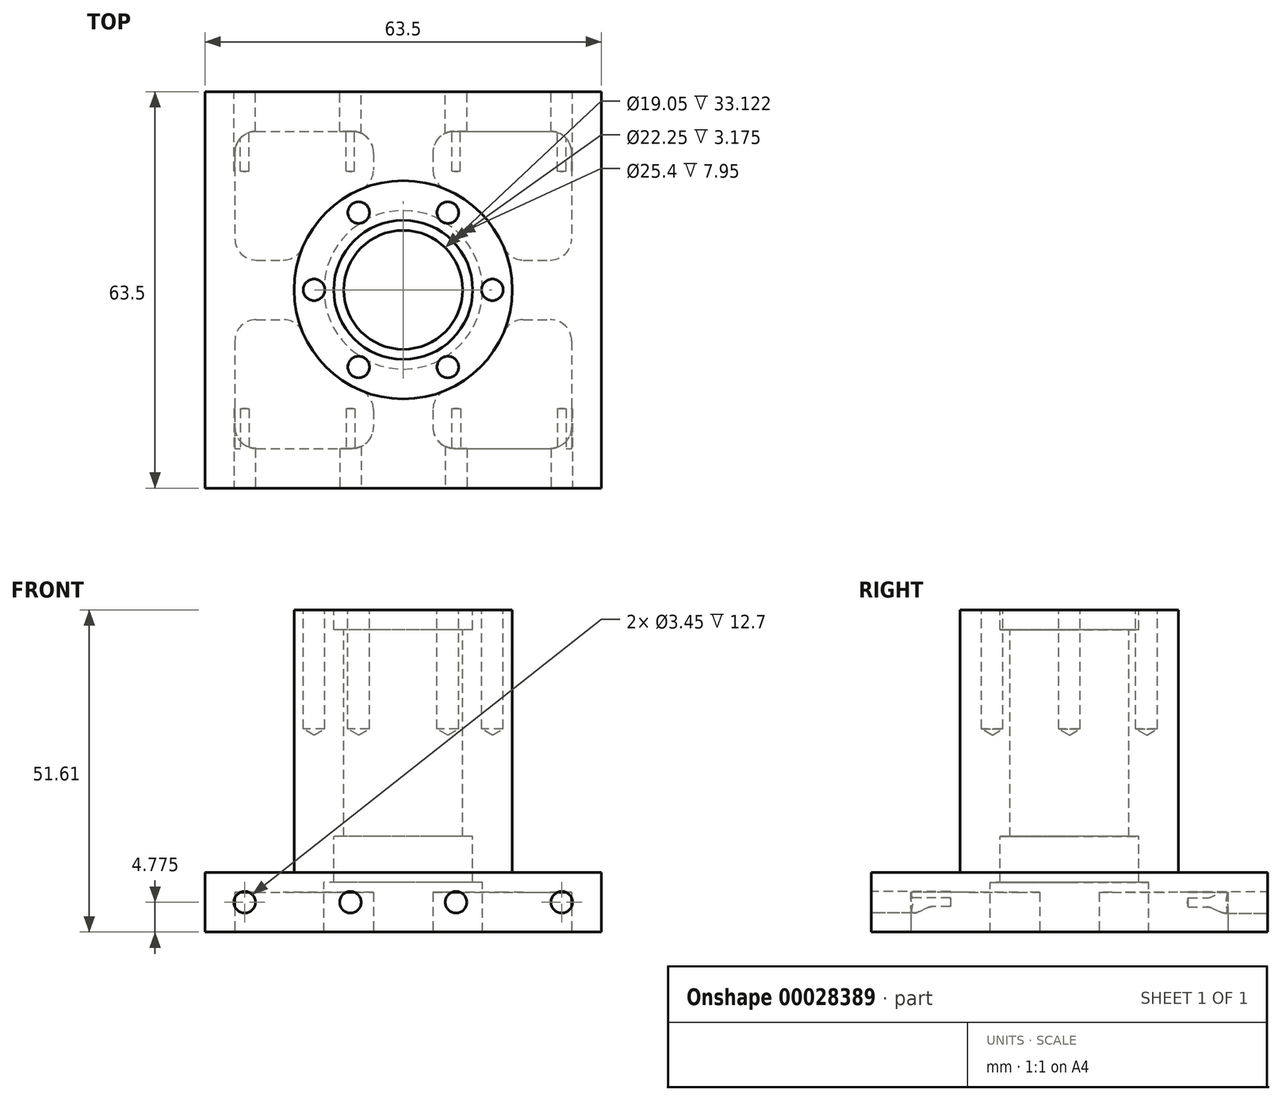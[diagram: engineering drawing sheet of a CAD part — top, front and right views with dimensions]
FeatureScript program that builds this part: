
annotation { "Feature Type Name" : "Feature", "Feature Type Description" : "" }
export const myFeature = defineFeature(function(context is Context, id is Id, definition is map)
    precondition{}
    {
        {
            var Q0;
            Q0=qCreatedBy(makeId("Front.planeOp"),FACE);
            var sketch = newSketch(context, id + "F0", { "sketchPlane" : qUnion([Q0])});
            skLineSegment(sketch, "E0", {"start": v(0, 39.17) * mm, "end": v(0, 0) * mm, "construction": true});
            skLineSegment(sketch, "E1", {"start": v(0, 0) * mm, "end": v(-12.7, 0) * mm, "construction": true});
            skLineSegment(sketch, "E2.bottom", {"start": v(-12.7, 0) * mm, "end": v(-45.72, 0) * mm});
            skLineSegment(sketch, "E2.top", {"start": v(-11.13, 51.61) * mm, "end": v(-17.49, 51.61) * mm});
            skLineSegment(sketch, "E2.left", {"start": v(-9.52, 15.32) * mm, "end": v(-9.53, 48.44) * mm});
            skLineSegment(sketch, "E2.right", {"start": v(-45.72, 0) * mm, "end": v(-45.72, 9.52) * mm});
            skLineSegment(sketch, "E3.top", {"start": v(-11.13, 48.44) * mm, "end": v(-9.53, 48.44) * mm});
            skLineSegment(sketch, "E3.left", {"start": v(-11.13, 51.61) * mm, "end": v(-11.13, 48.44) * mm});
            skLineSegment(sketch, "E4.bottom", {"start": v(-9.53, 15.32) * mm, "end": v(-11.13, 15.32) * mm});
            skLineSegment(sketch, "E4.right", {"start": v(-12.7, 7.95) * mm, "end": v(-12.7, 0) * mm});
            skLineSegment(sketch, "E5.bottom", {"start": v(-11.13, 7.95) * mm, "end": v(-12.7, 7.95) * mm});
            skLineSegment(sketch, "E5.left", {"start": v(-11.13, 7.95) * mm, "end": v(-11.13, 15.32) * mm});
            skLineSegment(sketch, "E6.bottom", {"start": v(-17.49, 9.53) * mm, "end": v(-45.72, 9.52) * mm});
            skLineSegment(sketch, "E6.left", {"start": v(-17.49, 9.53) * mm, "end": v(-17.49, 51.61) * mm});
            skSolve(sketch);
        }
        {
            var Q0;
            Q0=makeQuery(id+"F0.imprint","IMPRINT",FACE,{"disambiguationData":[TD([[makeQuery(id+"F0.imprint","IMPRINT",EDGE,{"derivedFrom":sQuery(id+"F0.wireOp",EDGE,"E2.bottom")}),-1.0]])]});
            var Q1;
            Q1=sQuery(id+"F0.wireOp",EDGE,"E0");
            revolve(context, id + "F1", {"entities" : qUnion([Q0]), "axis" : qUnion([Q1]), "revolveType" : RevolveType.FULL});
        }
        {
            var Q0;
            Q0=makeQuery(id+"F1.opRevolve","SWEPT_FACE",FACE,{"disambiguationData":[OSD([sQuery(id+"F0.wireOp",EDGE,"E2.bottom")])]});
            var sketch = newSketch(context, id + "F2", { "sketchPlane" : qUnion([Q0])});
            skLineSegment(sketch, "E7.rect.bottom", {"start": v(31.75, 31.75) * mm, "end": v(-31.75, 31.75) * mm});
            skLineSegment(sketch, "E7.rect.top", {"start": v(31.75, -31.75) * mm, "end": v(-31.75, -31.75) * mm});
            skLineSegment(sketch, "E7.rect.left", {"start": v(31.75, 31.75) * mm, "end": v(31.75, -31.75) * mm});
            skLineSegment(sketch, "E7.rect.right", {"start": v(-31.75, 31.75) * mm, "end": v(-31.75, -31.75) * mm});
            skPoint(sketch, "E7.rect.middle", {"position": v(0, 0) * mm});
            skSolve(sketch);
        }
        {
            var Q0;
            Q0=makeQuery(id+"F2.imprint","IMPRINT",FACE,{"disambiguationData":[TD([[makeQuery(id+"F2.imprint","IMPRINT",EDGE,{"derivedFrom":sQuery(id+"F2.wireOp",EDGE,"E7.rect.bottom")}),-1.0]])]});
            extrude(context, id + "F3", {"entities" : qUnion([Q0]), "operationType" : NewBodyOperationType.REMOVE, "endBound" : BoundingType.THROUGH_ALL, "oppositeDirection" : true, "depth" : 25.4 * mm});
        }
        {
            var Q0;
            Q0=makeQuery(id+"F3.boolean.opBoolean","COPY",FACE,{"derivedFrom":makeQuery(id+"F3.opExtrude","SWEPT_FACE",FACE,{"disambiguationData":[OSD([sQuery(id+"F2.wireOp",EDGE,"E7.rect.bottom")])]})});
            var sketch = newSketch(context, id + "F4", { "sketchPlane" : qUnion([Q0])});
            skLineSegment(sketch, "E8", {"start": v(-25.4, 4.78) * mm, "end": v(25.4, 4.78) * mm});
            skPoint(sketch, "E9", {"position": v(-8.47, 4.78) * mm});
            skPoint(sketch, "E10", {"position": v(8.47, 4.78) * mm});
            skLineSegment(sketch, "E11", {"start": v(0, 9.52) * mm, "end": v(0, -11.62) * mm});
            skSolve(sketch);
        }
        {
            var Q0;
            Q0=sQuery(id+"F4.wireOp",VERTEX,"E8.start");
            var Q1;
            Q1=sQuery(id+"F4.wireOp",VERTEX,"E9");
            var Q2;
            Q2=sQuery(id+"F4.wireOp",VERTEX,"E10");
            var Q3;
            Q3=sQuery(id+"F4.wireOp",VERTEX,"E8.end");
            var Q4;
            Q4=makeQuery(id+"F1.opRevolve","SWEPT_BODY",BODY,{"disambiguationData":[OSD([sQuery(id+"F0.wireOp",EDGE,"E2.bottom"),sQuery(id+"F0.wireOp",EDGE,"E2.top"),sQuery(id+"F0.wireOp",EDGE,"E2.left"),sQuery(id+"F0.wireOp",EDGE,"E2.right"),sQuery(id+"F0.wireOp",EDGE,"E3.top"),sQuery(id+"F0.wireOp",EDGE,"E3.left"),sQuery(id+"F0.wireOp",EDGE,"E4.bottom"),sQuery(id+"F0.wireOp",EDGE,"E4.right"),sQuery(id+"F0.wireOp",EDGE,"E5.bottom"),sQuery(id+"F0.wireOp",EDGE,"E5.left"),sQuery(id+"F0.wireOp",EDGE,"E6.bottom"),sQuery(id+"F0.wireOp",EDGE,"E6.left")])]});
            hole(context, id + "F5", {"style" : HoleStyle.SIMPLE, "holeDiameter" : 3.45 * mm, "endStyle" : HoleEndStyle.BLIND, "holeDepth" : 12.7 * mm, "locations" : qUnion([Q0, Q1, Q2, Q3]), "scope" : qUnion([Q4])});
        }
        {
            var Q0;
            Q0=makeQuery(id+"F1.opRevolve","SWEPT_FACE",FACE,{"disambiguationData":[OSD([sQuery(id+"F0.wireOp",EDGE,"E2.top")])]});
            var sketch = newSketch(context, id + "F6", { "sketchPlane" : qUnion([Q0])});
            skLineSegment(sketch, "E12", {"start": v(0, 0) * mm, "end": v(14.29, 0) * mm});
            skLineSegment(sketch, "E13.1.0", {"start": v(0, 0) * mm, "end": v(7.14, 12.37) * mm});
            skLineSegment(sketch, "E13.2.0", {"start": v(0, 0) * mm, "end": v(-7.14, 12.37) * mm});
            skLineSegment(sketch, "E13.3.0", {"start": v(0, 0) * mm, "end": v(-14.29, 0) * mm});
            skLineSegment(sketch, "E13.4.0", {"start": v(0, 0) * mm, "end": v(-7.14, -12.37) * mm});
            skLineSegment(sketch, "E13.5.0", {"start": v(0, 0) * mm, "end": v(7.14, -12.37) * mm});
            skPoint(sketch, "E13.center", {"position": v(0, 0) * mm});
            skSolve(sketch);
        }
        {
            var Q0;
            Q0=sQuery(id+"F6.wireOp",VERTEX,"E12.end");
            var Q1;
            Q1=sQuery(id+"F6.wireOp",VERTEX,"E13.5.0.end");
            var Q2;
            Q2=sQuery(id+"F6.wireOp",VERTEX,"E13.4.0.end");
            var Q3;
            Q3=sQuery(id+"F6.wireOp",VERTEX,"E13.3.0.end");
            var Q4;
            Q4=sQuery(id+"F6.wireOp",VERTEX,"E13.2.0.end");
            var Q5;
            Q5=sQuery(id+"F6.wireOp",VERTEX,"E13.1.0.end");
            var Q6;
            Q6=makeQuery(id+"F1.opRevolve","SWEPT_BODY",BODY,{"disambiguationData":[OSD([sQuery(id+"F0.wireOp",EDGE,"E2.bottom"),sQuery(id+"F0.wireOp",EDGE,"E2.top"),sQuery(id+"F0.wireOp",EDGE,"E2.left"),sQuery(id+"F0.wireOp",EDGE,"E2.right"),sQuery(id+"F0.wireOp",EDGE,"E3.top"),sQuery(id+"F0.wireOp",EDGE,"E3.left"),sQuery(id+"F0.wireOp",EDGE,"E4.bottom"),sQuery(id+"F0.wireOp",EDGE,"E4.right"),sQuery(id+"F0.wireOp",EDGE,"E5.bottom"),sQuery(id+"F0.wireOp",EDGE,"E5.left"),sQuery(id+"F0.wireOp",EDGE,"E6.bottom"),sQuery(id+"F0.wireOp",EDGE,"E6.left")])]});
            hole(context, id + "F7", {"style" : HoleStyle.SIMPLE, "holeDiameter" : 3.45 * mm, "endStyle" : HoleEndStyle.BLIND, "holeDepth" : 19.05 * mm, "locations" : qUnion([Q0, Q1, Q2, Q3, Q4, Q5]), "scope" : qUnion([Q6])});
        }
        {
            var Q0;
            Q0=makeQuery(id+"F1.opRevolve","SWEPT_FACE",FACE,{"disambiguationData":[OSD([sQuery(id+"F0.wireOp",EDGE,"E2.bottom")])]});
            var sketch = newSketch(context, id + "F8", { "sketchPlane" : qUnion([Q0])});
            skLineSegment(sketch, "E14.rect.bottom", {"start": v(-26.97, -25.4) * mm, "end": v(-4.76, -25.4) * mm});
            skLineSegment(sketch, "E14.rect.top", {"start": v(-26.97, 25.4) * mm, "end": v(-4.76, 25.4) * mm});
            skLineSegment(sketch, "E14.rect.left", {"start": v(-26.97, -25.4) * mm, "end": v(-26.97, -4.76) * mm});
            skLineSegment(sketch, "E14.rect.right", {"start": v(26.97, -25.4) * mm, "end": v(26.97, -4.76) * mm});
            skPoint(sketch, "E14.rect.middle", {"position": v(0, 0) * mm});
            skArc(sketch, "E15", {"start": v(-4.76, 16.81) * mm, "mid": v(-12.36, 12.36) * mm, "end": v(-16.81, 4.76) * mm});
            skLineSegment(sketch, "E16", {"start": v(-33.58, 0) * mm, "end": v(0, 0) * mm, "construction": true});
            skLineSegment(sketch, "E17", {"start": v(0, 36.76) * mm, "end": v(0, 0) * mm, "construction": true});
            skLineSegment(sketch, "E18.bottom", {"start": v(-26.97, -4.76) * mm, "end": v(-16.81, -4.76) * mm});
            skLineSegment(sketch, "E18.top", {"start": v(-26.97, 4.76) * mm, "end": v(-16.81, 4.76) * mm});
            skLineSegment(sketch, "E19.left", {"start": v(-4.76, 16.81) * mm, "end": v(-4.76, 25.4) * mm});
            skLineSegment(sketch, "E19.right", {"start": v(4.76, 16.81) * mm, "end": v(4.76, 25.4) * mm});
            skLineSegment(sketch, "E20.bottom", {"start": v(16.81, 4.76) * mm, "end": v(26.97, 4.76) * mm});
            skLineSegment(sketch, "E20.top", {"start": v(16.81, -4.76) * mm, "end": v(26.97, -4.76) * mm});
            skLineSegment(sketch, "E21.left", {"start": v(-4.76, -25.4) * mm, "end": v(-4.76, -16.81) * mm});
            skLineSegment(sketch, "E21.right", {"start": v(4.76, -25.4) * mm, "end": v(4.76, -16.81) * mm});
            skLineSegment(sketch, "E22.trimOffspring", {"start": v(4.76, 25.4) * mm, "end": v(26.97, 25.4) * mm});
            skArc(sketch, "E23.trimOffspring", {"start": v(16.81, 4.76) * mm, "mid": v(12.36, 12.36) * mm, "end": v(4.76, 16.81) * mm});
            skLineSegment(sketch, "E24.trimOffspring", {"start": v(4.76, -25.4) * mm, "end": v(26.97, -25.4) * mm});
            skArc(sketch, "E25.trimOffspring", {"start": v(4.76, -16.81) * mm, "mid": v(12.36, -12.36) * mm, "end": v(16.81, -4.76) * mm});
            skLineSegment(sketch, "E26.trimOffspring", {"start": v(-26.97, 4.76) * mm, "end": v(-26.97, 25.4) * mm});
            skArc(sketch, "E27.trimOffspring", {"start": v(-16.81, -4.76) * mm, "mid": v(-12.36, -12.36) * mm, "end": v(-4.76, -16.81) * mm});
            skLineSegment(sketch, "E28.trimOffspring", {"start": v(26.97, 4.76) * mm, "end": v(26.97, 25.4) * mm});
            skSolve(sketch);
        }
        {
            var Q0;
            Q0=makeQuery(id+"F8.imprint","IMPRINT",FACE,{"disambiguationData":[TD([[makeQuery(id+"F8.imprint","IMPRINT",EDGE,{"derivedFrom":sQuery(id+"F8.wireOp",EDGE,"E14.rect.bottom")}),1.0]])]});
            var Q1;
            Q1=makeQuery(id+"F8.imprint","IMPRINT",FACE,{"disambiguationData":[TD([[makeQuery(id+"F8.imprint","IMPRINT",EDGE,{"derivedFrom":sQuery(id+"F8.wireOp",EDGE,"E14.rect.top")}),-1.0]])]});
            var Q2;
            Q2=makeQuery(id+"F8.imprint","IMPRINT",FACE,{"disambiguationData":[TD([[makeQuery(id+"F8.imprint","IMPRINT",EDGE,{"derivedFrom":sQuery(id+"F8.wireOp",EDGE,"E19.right")}),-1.0]])]});
            var Q3;
            Q3=makeQuery(id+"F8.imprint","IMPRINT",FACE,{"disambiguationData":[TD([[makeQuery(id+"F8.imprint","IMPRINT",EDGE,{"derivedFrom":sQuery(id+"F8.wireOp",EDGE,"E14.rect.right")}),1.0]])]});
            extrude(context, id + "F9", {"entities" : qUnion([Q0, Q1, Q2, Q3]), "operationType" : NewBodyOperationType.REMOVE, "oppositeDirection" : true, "depth" : 6.35 * mm});
        }
        {
            var Q0;
            Q0=makeQuery(id+"F9.boolean.opBoolean","COPY",EDGE,{"derivedFrom":makeQuery(id+"F9.opExtrude","SWEPT_EDGE",EDGE,{"disambiguationData":[OSD([sQuery(id+"F8.wireOp",EDGE,"E14.rect.bottom"),sQuery(id+"F8.wireOp",EDGE,"E21.left")])]})});
            var Q1;
            Q1=makeQuery(id+"F9.boolean.opBoolean","COPY",EDGE,{"derivedFrom":makeQuery(id+"F9.opExtrude","SWEPT_EDGE",EDGE,{"disambiguationData":[OSD([sQuery(id+"F8.wireOp",EDGE,"E21.left"),sQuery(id+"F8.wireOp",EDGE,"E27.trimOffspring")])]})});
            var Q2;
            Q2=makeQuery(id+"F9.boolean.opBoolean","COPY",EDGE,{"derivedFrom":makeQuery(id+"F9.opExtrude","SWEPT_EDGE",EDGE,{"disambiguationData":[OSD([sQuery(id+"F8.wireOp",EDGE,"E18.bottom"),sQuery(id+"F8.wireOp",EDGE,"E27.trimOffspring")])]})});
            var Q3;
            Q3=makeQuery(id+"F9.boolean.opBoolean","COPY",EDGE,{"derivedFrom":makeQuery(id+"F9.opExtrude","SWEPT_EDGE",EDGE,{"disambiguationData":[OSD([sQuery(id+"F8.wireOp",EDGE,"E14.rect.left"),sQuery(id+"F8.wireOp",EDGE,"E18.bottom")])]})});
            var Q4;
            Q4=makeQuery(id+"F9.boolean.opBoolean","COPY",EDGE,{"derivedFrom":makeQuery(id+"F9.opExtrude","SWEPT_EDGE",EDGE,{"disambiguationData":[OSD([sQuery(id+"F8.wireOp",EDGE,"E14.rect.bottom"),sQuery(id+"F8.wireOp",EDGE,"E14.rect.left")])]})});
            var Q5;
            Q5=makeQuery(id+"F9.boolean.opBoolean","COPY",EDGE,{"derivedFrom":makeQuery(id+"F9.opExtrude","SWEPT_EDGE",EDGE,{"disambiguationData":[OSD([sQuery(id+"F8.wireOp",EDGE,"E18.top"),sQuery(id+"F8.wireOp",EDGE,"E26.trimOffspring")])]})});
            var Q6;
            Q6=makeQuery(id+"F9.boolean.opBoolean","COPY",EDGE,{"derivedFrom":makeQuery(id+"F9.opExtrude","SWEPT_EDGE",EDGE,{"disambiguationData":[OSD([sQuery(id+"F8.wireOp",EDGE,"E21.right"),sQuery(id+"F8.wireOp",EDGE,"E24.trimOffspring")])]})});
            var Q7;
            Q7=makeQuery(id+"F9.boolean.opBoolean","COPY",EDGE,{"derivedFrom":makeQuery(id+"F9.opExtrude","SWEPT_EDGE",EDGE,{"disambiguationData":[OSD([sQuery(id+"F8.wireOp",EDGE,"E20.bottom"),sQuery(id+"F8.wireOp",EDGE,"E23.trimOffspring")])]})});
            var Q8;
            Q8=makeQuery(id+"F9.boolean.opBoolean","COPY",EDGE,{"derivedFrom":makeQuery(id+"F9.opExtrude","SWEPT_EDGE",EDGE,{"disambiguationData":[OSD([sQuery(id+"F8.wireOp",EDGE,"E19.right"),sQuery(id+"F8.wireOp",EDGE,"E23.trimOffspring")])]})});
            var Q9;
            Q9=makeQuery(id+"F9.boolean.opBoolean","COPY",EDGE,{"derivedFrom":makeQuery(id+"F9.opExtrude","SWEPT_EDGE",EDGE,{"disambiguationData":[OSD([sQuery(id+"F8.wireOp",EDGE,"E15"),sQuery(id+"F8.wireOp",EDGE,"E19.left")])]})});
            var Q10;
            Q10=makeQuery(id+"F9.boolean.opBoolean","COPY",EDGE,{"derivedFrom":makeQuery(id+"F9.opExtrude","SWEPT_EDGE",EDGE,{"disambiguationData":[OSD([sQuery(id+"F8.wireOp",EDGE,"E15"),sQuery(id+"F8.wireOp",EDGE,"E18.top")])]})});
            var Q11;
            Q11=makeQuery(id+"F9.boolean.opBoolean","COPY",EDGE,{"derivedFrom":makeQuery(id+"F9.opExtrude","SWEPT_EDGE",EDGE,{"disambiguationData":[OSD([sQuery(id+"F8.wireOp",EDGE,"E14.rect.right"),sQuery(id+"F8.wireOp",EDGE,"E24.trimOffspring")])]})});
            var Q12;
            Q12=makeQuery(id+"F9.boolean.opBoolean","COPY",EDGE,{"derivedFrom":makeQuery(id+"F9.opExtrude","SWEPT_EDGE",EDGE,{"disambiguationData":[OSD([sQuery(id+"F8.wireOp",EDGE,"E20.bottom"),sQuery(id+"F8.wireOp",EDGE,"E28.trimOffspring")])]})});
            var Q13;
            {var subQ0=sQuery(id+"F8.wireOp",EDGE,"E14.rect.top");var subQ1=sQuery(id+"F8.wireOp",EDGE,"E26.trimOffspring");Q13=makeQuery(id+"F9.boolean.opBoolean","COPY",EDGE,{"disambiguationData":[TD([makeQuery(id+"F1.opRevolve","SWEPT_FACE",FACE,{"disambiguationData":[OSD([sQuery(id+"F0.wireOp",EDGE,"E2.bottom")])]})])],"derivedFrom":makeQuery(id+"F9.opExtrude","SWEPT_EDGE",EDGE,{"disambiguationData":[OSD([subQ0,subQ1])]})});}
            var Q14;
            Q14=makeQuery(id+"F9.boolean.opBoolean","COPY",EDGE,{"derivedFrom":makeQuery(id+"F9.opExtrude","SWEPT_EDGE",EDGE,{"disambiguationData":[OSD([sQuery(id+"F8.wireOp",EDGE,"E14.rect.top"),sQuery(id+"F8.wireOp",EDGE,"E19.left")])]})});
            var Q15;
            {var subQ0=sQuery(id+"F8.wireOp",EDGE,"E28.trimOffspring");var subQ1=sQuery(id+"F8.wireOp",EDGE,"E22.trimOffspring");Q15=makeQuery(id+"F9.boolean.opBoolean","COPY",EDGE,{"disambiguationData":[TD([makeQuery(id+"F1.opRevolve","SWEPT_FACE",FACE,{"disambiguationData":[OSD([sQuery(id+"F0.wireOp",EDGE,"E2.bottom")])]})])],"derivedFrom":makeQuery(id+"F9.opExtrude","SWEPT_EDGE",EDGE,{"disambiguationData":[OSD([subQ1,subQ0])]})});}
            var Q16;
            Q16=makeQuery(id+"F9.boolean.opBoolean","COPY",EDGE,{"derivedFrom":makeQuery(id+"F9.opExtrude","SWEPT_EDGE",EDGE,{"disambiguationData":[OSD([sQuery(id+"F8.wireOp",EDGE,"E19.right"),sQuery(id+"F8.wireOp",EDGE,"E22.trimOffspring")])]})});
            var Q17;
            Q17=makeQuery(id+"F9.boolean.opBoolean","COPY",EDGE,{"derivedFrom":makeQuery(id+"F9.opExtrude","SWEPT_EDGE",EDGE,{"disambiguationData":[OSD([sQuery(id+"F8.wireOp",EDGE,"E20.top"),sQuery(id+"F8.wireOp",EDGE,"E25.trimOffspring")])]})});
            var Q18;
            Q18=makeQuery(id+"F9.boolean.opBoolean","COPY",EDGE,{"derivedFrom":makeQuery(id+"F9.opExtrude","SWEPT_EDGE",EDGE,{"disambiguationData":[OSD([sQuery(id+"F8.wireOp",EDGE,"E21.right"),sQuery(id+"F8.wireOp",EDGE,"E25.trimOffspring")])]})});
            var Q19;
            Q19=makeQuery(id+"F9.boolean.opBoolean","COPY",EDGE,{"derivedFrom":makeQuery(id+"F9.opExtrude","SWEPT_EDGE",EDGE,{"disambiguationData":[OSD([sQuery(id+"F8.wireOp",EDGE,"E14.rect.right"),sQuery(id+"F8.wireOp",EDGE,"E20.top")])]})});
            fillet(context, id + "F10", {"entities" : qUnion([Q0, Q1, Q2, Q3, Q4, Q5, Q6, Q7, Q8, Q9, Q10, Q11, Q12, Q13, Q14, Q15, Q16, Q17, Q18, Q19]), "radius" : 3.43 * mm, "tangentPropagation" : true, "allowEdgeOverflow" : false});
        }
        {
            var Q0;
            Q0=makeQuery(id+"F3.boolean.opBoolean","COPY",FACE,{"derivedFrom":makeQuery(id+"F3.opExtrude","SWEPT_FACE",FACE,{"disambiguationData":[OSD([sQuery(id+"F2.wireOp",EDGE,"E7.rect.top")])]})});
            var sketch = newSketch(context, id + "F11", { "sketchPlane" : qUnion([Q0])});
            skLineSegment(sketch, "E29", {"start": v(-25.4, 4.76) * mm, "end": v(25.4, 4.76) * mm});
            skPoint(sketch, "E30", {"position": v(-8.47, 4.76) * mm});
            skPoint(sketch, "E31", {"position": v(8.47, 4.76) * mm});
            skLineSegment(sketch, "E32", {"start": v(0, 9.52) * mm, "end": v(0, -12.08) * mm});
            skSolve(sketch);
        }
        {
            var Q0;
            Q0=sQuery(id+"F11.wireOp",VERTEX,"E29.start");
            var Q1;
            Q1=sQuery(id+"F11.wireOp",VERTEX,"E30");
            var Q2;
            Q2=sQuery(id+"F11.wireOp",VERTEX,"E31");
            var Q3;
            Q3=sQuery(id+"F11.wireOp",VERTEX,"E29.end");
            var Q4;
            Q4=makeQuery(id+"F1.opRevolve","SWEPT_BODY",BODY,{"disambiguationData":[OSD([sQuery(id+"F0.wireOp",EDGE,"E2.bottom"),sQuery(id+"F0.wireOp",EDGE,"E2.top"),sQuery(id+"F0.wireOp",EDGE,"E2.left"),sQuery(id+"F0.wireOp",EDGE,"E2.right"),sQuery(id+"F0.wireOp",EDGE,"E3.top"),sQuery(id+"F0.wireOp",EDGE,"E3.left"),sQuery(id+"F0.wireOp",EDGE,"E4.bottom"),sQuery(id+"F0.wireOp",EDGE,"E4.right"),sQuery(id+"F0.wireOp",EDGE,"E5.bottom"),sQuery(id+"F0.wireOp",EDGE,"E5.left"),sQuery(id+"F0.wireOp",EDGE,"E6.bottom"),sQuery(id+"F0.wireOp",EDGE,"E6.left")])]});
            hole(context, id + "F12", {"style" : HoleStyle.SIMPLE, "holeDiameter" : 3.45 * mm, "endStyle" : HoleEndStyle.BLIND, "holeDepth" : 12.7 * mm, "locations" : qUnion([Q0, Q1, Q2, Q3]), "scope" : qUnion([Q4])});
        }
    });
